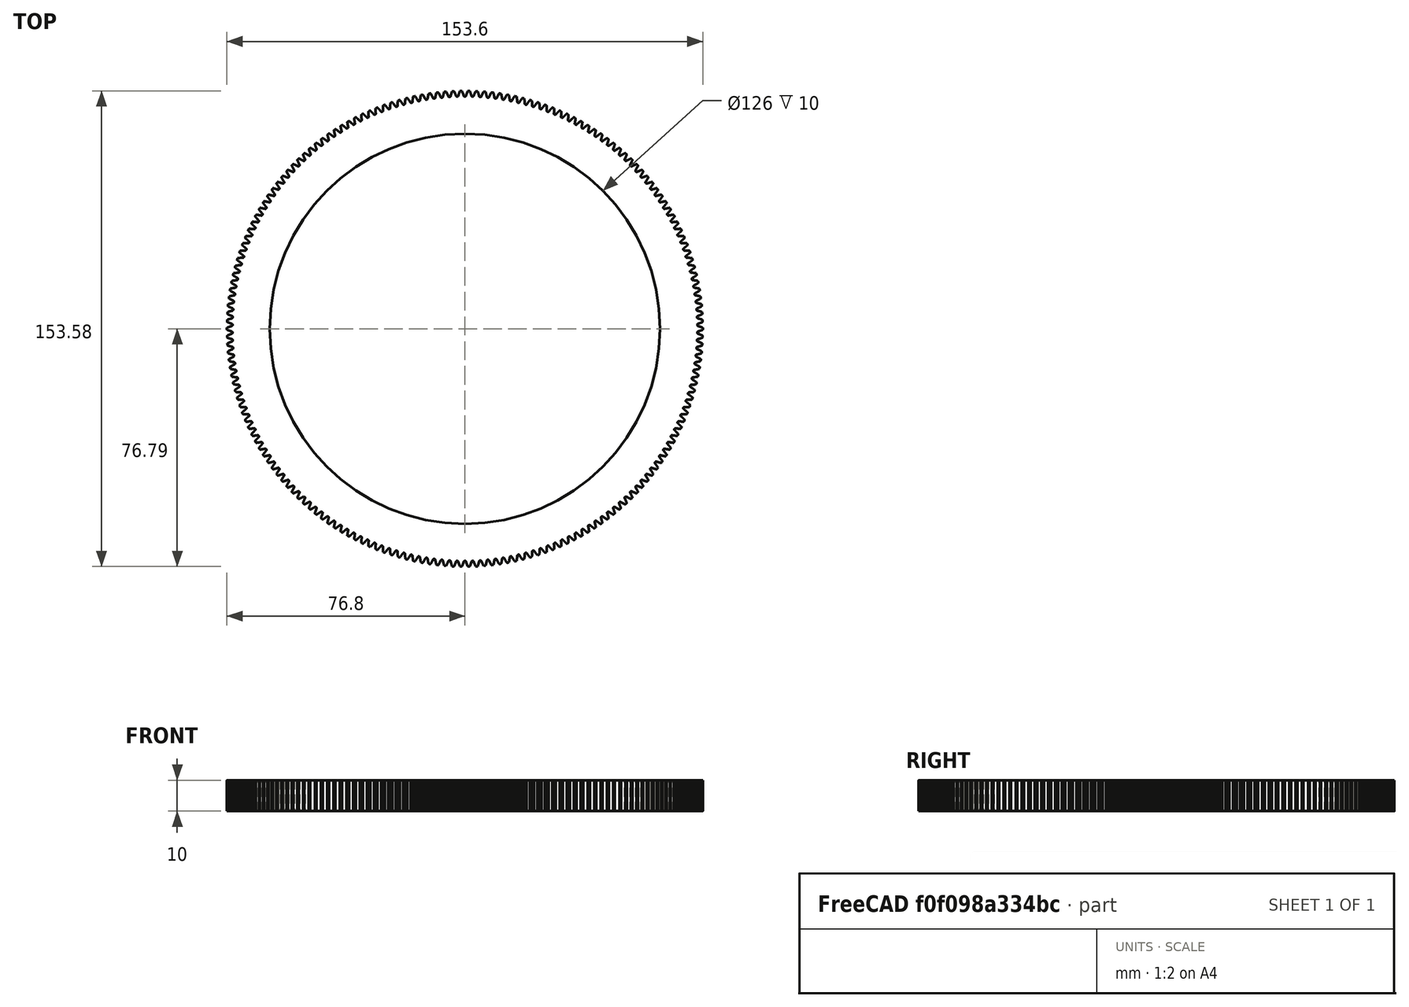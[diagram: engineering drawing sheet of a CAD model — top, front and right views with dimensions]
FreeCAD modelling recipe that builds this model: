
FCSTD DOCUMENT  (FreeCAD 0.15R4671 (Git))
Label: lomo-35opf-1-ff
License: All rights reserved
LicenseURL: http://en.wikipedia.org/wiki/All_rights_reserved
objects: Drawing::FeatureViewPart×3, Part::Part2DObjectPython×1, PartDesign::Pad×1, Part::Cylinder×1, Part::Cut×1, Drawing::FeaturePage×1
note: 5 computed .brp shape members not serialized (recipe doc carries the construction recipe); baked Part::Feature solids carry a one-line shape summary decoded from their .brp

FEATURE [Part::Part2DObjectPython] InvoluteGear  # Draft 2D object (typed FeaturePython)
  ExternalGear = true
  HighPrecision = true
  Modules = 0.8
  NumberOfTeeth = 190
  PressureAngle = 20
FEATURE [PartDesign::Pad] Pad
  Length = 10
  Length2 = 100
  Sketch = -> InvoluteGear
  Type = 0
FEATURE [Part::Cylinder] Cylinder
  Angle = 360
  Height = 10
  Radius = 63
FEATURE [Part::Cut] Cut  label="Final"
  Base = -> Pad
  Tool = -> Cylinder
FEATURE [Drawing::FeatureViewPart] topView
  Direction = (0,0,1)
  HiddenWidth = 0.15
  LineWidth = 0.35
  Rotation = 180
  ShowHiddenLines = true
  ShowSmoothLines = false
  Source = -> Cut
  Tolerance = 0.05
  ViewResult = <blob: 218942 chars omitted>
  Visible = true
  X = 115
  Y = 130
FEATURE [Drawing::FeatureViewPart] RightView
  Direction = (1,0,0)
  HiddenWidth = 0.15
  LineWidth = 0.35
  Rotation = 0
  ShowHiddenLines = true
  ShowSmoothLines = false
  Source = -> Cut
  Tolerance = 0.05
  ViewResult = <blob: 551765 chars omitted>
  Visible = true
  X = 225
  Y = 130
FEATURE [Drawing::FeatureViewPart] IsoView
  Direction = (1,1,1)
  HiddenWidth = 0.15
  LineWidth = 0.35
  Rotation = 60
  ShowHiddenLines = true
  ShowSmoothLines = false
  Source = -> Cut
  Tolerance = 0.05
  ViewResult = <blob: 370724 chars omitted>
  Visible = true
  X = 330
  Y = 130
FEATURE [Drawing::FeaturePage] AutoDrawing  label="Drawing"
  EditableTexts = FLOYD DIEBEL | 5/30/2015 | 1:1 | 1 | LOMO FOCUS GEAR | FOR 20-120 mm 35 OPF-18-1
  Group = -> [topView,RightView,IsoView]
  Template = C:/Program Files/FreeCAD 0.15/data/Mod/Drawing/Templates/A3_Landscape.svg
